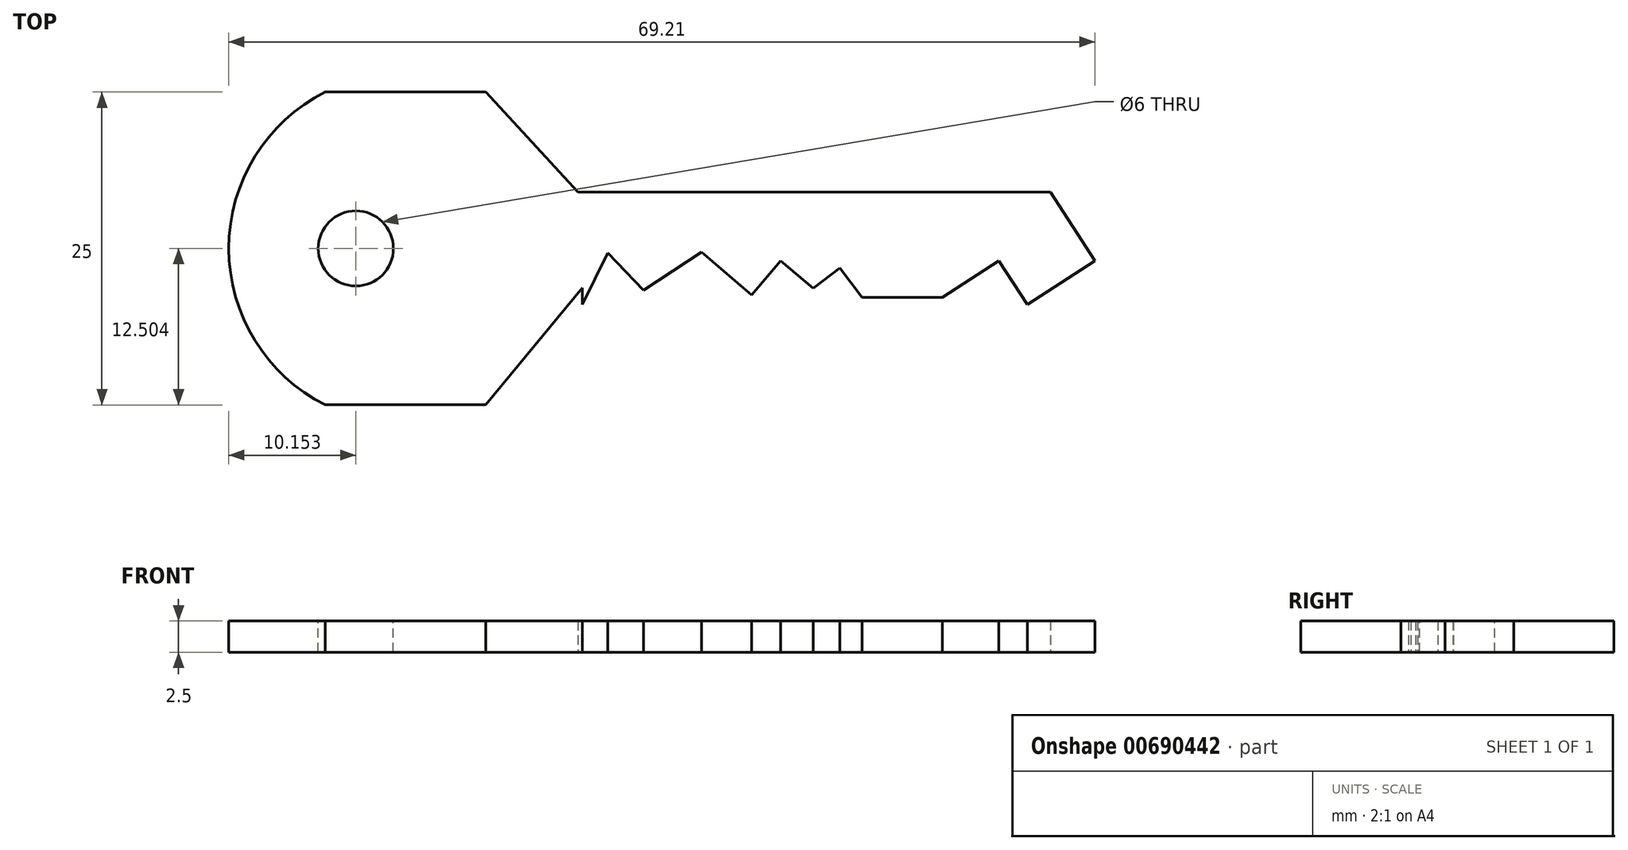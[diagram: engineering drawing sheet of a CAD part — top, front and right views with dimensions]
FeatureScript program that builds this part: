
annotation { "Feature Type Name" : "Feature", "Feature Type Description" : "" }
export const myFeature = defineFeature(function(context is Context, id is Id, definition is map)
    precondition{}
    {
        {
            var Q0;
            Q0=qCreatedBy(makeId("Top.planeOp"),FACE);
            var sketch = newSketch(context, id + "F0", { "sketchPlane" : qUnion([Q0])});
            skLineSegment(sketch, "E0", {"start": v(5.68, 13.48) * mm, "end": v(18.5, 13.48) * mm});
            skLineSegment(sketch, "E1", {"start": v(18.5, 13.48) * mm, "end": v(25.86, 5.48) * mm});
            skLineSegment(sketch, "E2", {"start": v(25.86, 5.48) * mm, "end": v(63.62, 5.48) * mm});
            skLineSegment(sketch, "E3", {"start": v(63.62, 5.48) * mm, "end": v(67.18, 0) * mm});
            skLineSegment(sketch, "E4", {"start": v(67.18, 0) * mm, "end": v(61.77, -3.52) * mm});
            skLineSegment(sketch, "E5", {"start": v(61.77, -3.52) * mm, "end": v(59.48, 0) * mm});
            skLineSegment(sketch, "E6", {"start": v(59.48, 0) * mm, "end": v(54.98, -2.92) * mm});
            skLineSegment(sketch, "E7", {"start": v(54.98, -2.92) * mm, "end": v(48.57, -2.92) * mm});
            skLineSegment(sketch, "E8", {"start": v(48.57, -2.92) * mm, "end": v(46.8, -0.58) * mm});
            skLineSegment(sketch, "E9", {"start": v(46.8, -0.58) * mm, "end": v(44.66, -2.2) * mm});
            skLineSegment(sketch, "E10", {"start": v(44.66, -2.2) * mm, "end": v(42.06, 0) * mm});
            skLineSegment(sketch, "E11", {"start": v(42.06, 0) * mm, "end": v(39.75, -2.72) * mm});
            skLineSegment(sketch, "E12", {"start": v(39.75, -2.72) * mm, "end": v(35.73, 0.68) * mm});
            skLineSegment(sketch, "E13", {"start": v(35.73, 0.68) * mm, "end": v(31.12, -2.35) * mm});
            skLineSegment(sketch, "E14", {"start": v(31.12, -2.35) * mm, "end": v(28.25, 0.64) * mm});
            skLineSegment(sketch, "E15", {"start": v(28.25, 0.64) * mm, "end": v(26.23, -3.52) * mm});
            skLineSegment(sketch, "E16", {"start": v(26.23, -3.52) * mm, "end": v(26.23, -2.18) * mm});
            skLineSegment(sketch, "E17", {"start": v(26.23, -2.18) * mm, "end": v(18.5, -11.52) * mm});
            skLineSegment(sketch, "E18", {"start": v(18.5, -11.52) * mm, "end": v(5.68, -11.52) * mm});
            skArc(sketch, "E19", {"start": v(5.68, 13.48) * mm, "mid": v(-2.03, 0.98) * mm, "end": v(5.68, -11.52) * mm});
            skPoint(sketch, "E20.end.orphan", {"position": v(-5.75, 0) * mm});
            skSolve(sketch);
        }
        {
            var Q0;
            Q0 = qSketchRegion(id + "F0", true);
            extrude(context, id + "F1", {"entities" : qUnion([Q0]), "depth" : 2.5 * mm, "offsetDistance" : 25 * mm});
        }
        {
            var Q0;
            Q0=makeQuery(id+"F1.opExtrude","CAP_FACE",FACE,{"disambiguationData":[OSD([sQuery(id+"F0.wireOp",EDGE,"E0"),sQuery(id+"F0.wireOp",EDGE,"E1"),sQuery(id+"F0.wireOp",EDGE,"E2"),sQuery(id+"F0.wireOp",EDGE,"E3"),sQuery(id+"F0.wireOp",EDGE,"E4"),sQuery(id+"F0.wireOp",EDGE,"E5"),sQuery(id+"F0.wireOp",EDGE,"E6"),sQuery(id+"F0.wireOp",EDGE,"E7"),sQuery(id+"F0.wireOp",EDGE,"E8"),sQuery(id+"F0.wireOp",EDGE,"E9"),sQuery(id+"F0.wireOp",EDGE,"E10"),sQuery(id+"F0.wireOp",EDGE,"E11"),sQuery(id+"F0.wireOp",EDGE,"E12"),sQuery(id+"F0.wireOp",EDGE,"E13"),sQuery(id+"F0.wireOp",EDGE,"E14"),sQuery(id+"F0.wireOp",EDGE,"E15"),sQuery(id+"F0.wireOp",EDGE,"E16"),sQuery(id+"F0.wireOp",EDGE,"E17"),sQuery(id+"F0.wireOp",EDGE,"E18"),sQuery(id+"F0.wireOp",EDGE,"E19")])],"isStart":false});
            var sketch = newSketch(context, id + "F2", { "sketchPlane" : qUnion([Q0])});
            skCircle(sketch, "E21", {"center": v(8.12, 0.98) * mm, "radius": 3 * mm});
            skSolve(sketch);
        }
        {
            var Q0;
            Q0 = qSketchRegion(id + "F2", true);
            extrude(context, id + "F3", {"entities" : qUnion([Q0]), "operationType" : NewBodyOperationType.REMOVE, "oppositeDirection" : true, "depth" : 25 * mm, "offsetDistance" : 25 * mm});
        }
    });
